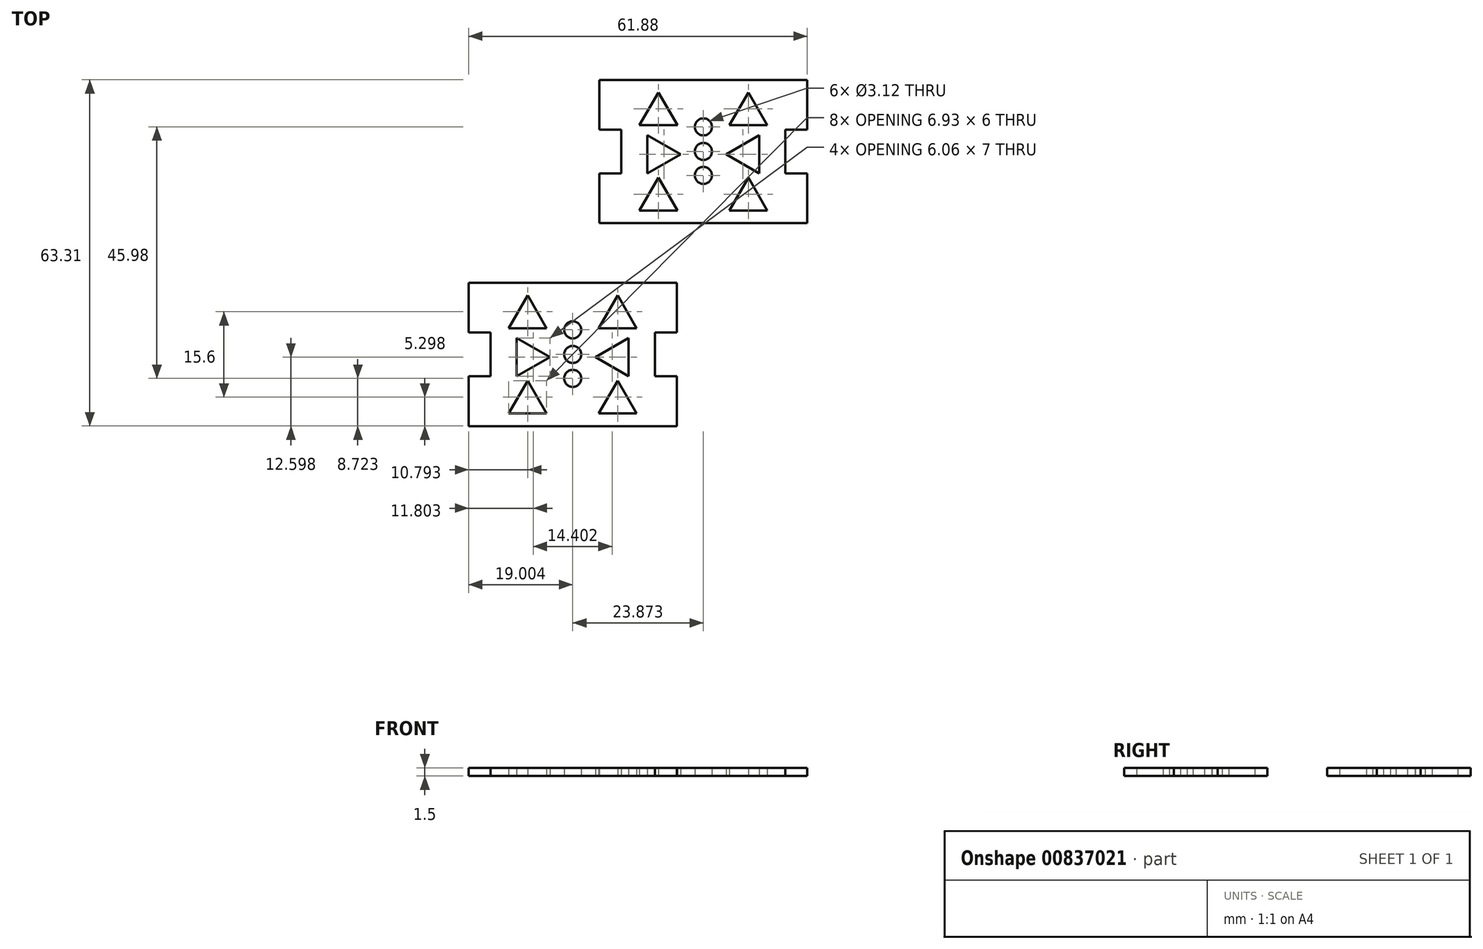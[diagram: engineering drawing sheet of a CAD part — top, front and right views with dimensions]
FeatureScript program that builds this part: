
annotation { "Feature Type Name" : "Feature", "Feature Type Description" : "" }
export const myFeature = defineFeature(function(context is Context, id is Id, definition is map)
    precondition{}
    {
        {
            var Q0;
            Q0=qCreatedBy(makeId("Top.planeOp"),FACE);
            var sketch = newSketch(context, id + "F0", { "sketchPlane" : qUnion([Q0])});
            skLineSegment(sketch, "E0.bottom", {"start": v(-70.41, 59.77) * mm, "end": v(-66.41, 59.77) * mm});
            skLineSegment(sketch, "E0.top", {"start": v(-70.41, 50.67) * mm, "end": v(-66.41, 50.67) * mm});
            skLineSegment(sketch, "E0.left", {"start": v(-70.41, 59.77) * mm, "end": v(-70.41, 50.67) * mm});
            skLineSegment(sketch, "E0.right", {"start": v(-66.41, 59.77) * mm, "end": v(-66.41, 50.67) * mm});
            skLineSegment(sketch, "E1", {"start": v(-66.41, 50.67) * mm, "end": v(-66.41, 42.67) * mm});
            skLineSegment(sketch, "E2.bottom", {"start": v(-70.41, 42.67) * mm, "end": v(-66.41, 42.67) * mm});
            skLineSegment(sketch, "E2.top", {"start": v(-70.41, 33.57) * mm, "end": v(-66.41, 33.57) * mm});
            skLineSegment(sketch, "E2.left", {"start": v(-70.41, 42.67) * mm, "end": v(-70.41, 33.57) * mm});
            skLineSegment(sketch, "E2.right", {"start": v(-66.41, 42.67) * mm, "end": v(-66.41, 33.57) * mm});
            skLineSegment(sketch, "E3.bottom", {"start": v(-66.41, 59.77) * mm, "end": v(-51.41, 59.77) * mm});
            skLineSegment(sketch, "E3.top", {"start": v(-66.41, 33.57) * mm, "end": v(-51.41, 33.57) * mm});
            skLineSegment(sketch, "E3.left", {"start": v(-66.41, 59.77) * mm, "end": v(-66.41, 33.57) * mm});
            skArc(sketch, "E4", {"start": v(-51.41, 52.73) * mm, "mid": v(-52.98, 51.16) * mm, "end": v(-51.41, 49.6) * mm});
            skArc(sketch, "E5", {"start": v(-51.41, 43.85) * mm, "mid": v(-52.98, 42.3) * mm, "end": v(-51.41, 40.73) * mm});
            skArc(sketch, "E6", {"start": v(-51.41, 48.23) * mm, "mid": v(-52.98, 46.67) * mm, "end": v(-51.41, 45.1) * mm});
            skLineSegment(sketch, "E7", {"start": v(-51.41, 59.77) * mm, "end": v(-51.41, 33.57) * mm});
            skPoint(sketch, "E3.right.end.orphan", {"position": v(-36.41, 33.57) * mm});
            skPoint(sketch, "E8.orphan", {"position": v(-36.41, 59.77) * mm});
            skCircle(sketch, "E9.cCircle", {"center": v(-59.62, 53.47) * mm, "radius": 2 * mm, "construction": true});
            skLineSegment(sketch, "E9.0", {"start": v(-56.16, 51.47) * mm, "end": v(-63.09, 51.47) * mm});
            skLineSegment(sketch, "E9.1", {"start": v(-63.09, 51.47) * mm, "end": v(-59.62, 57.47) * mm});
            skLineSegment(sketch, "E9.2", {"start": v(-59.62, 57.47) * mm, "end": v(-56.16, 51.47) * mm});
            skPoint(sketch, "E9.0.midPoint", {"position": v(-59.62, 51.47) * mm});
            skCircle(sketch, "E10.cCircle", {"center": v(-59.62, 37.87) * mm, "radius": 2 * mm, "construction": true});
            skLineSegment(sketch, "E10.0", {"start": v(-56.16, 35.87) * mm, "end": v(-63.09, 35.87) * mm});
            skLineSegment(sketch, "E10.1", {"start": v(-63.09, 35.87) * mm, "end": v(-59.62, 41.87) * mm});
            skLineSegment(sketch, "E10.2", {"start": v(-59.62, 41.87) * mm, "end": v(-56.16, 35.87) * mm});
            skPoint(sketch, "E10.0.midPoint", {"position": v(-59.62, 35.87) * mm});
            skCircle(sketch, "E11.cCircle", {"center": v(-59.62, 46.17) * mm, "radius": 2.02 * mm, "construction": true});
            skLineSegment(sketch, "E11.0", {"start": v(-55.58, 46.17) * mm, "end": v(-61.65, 42.67) * mm});
            skLineSegment(sketch, "E11.1", {"start": v(-61.65, 42.67) * mm, "end": v(-61.65, 49.67) * mm});
            skLineSegment(sketch, "E11.2", {"start": v(-61.65, 49.67) * mm, "end": v(-55.58, 46.17) * mm});
            skPoint(sketch, "E11.0.midPoint", {"position": v(-58.61, 44.42) * mm});
            skLineSegment(sketch, "E12.MirrorCS", {"start": v(-36.41, 59.77) * mm, "end": v(-36.41, 50.67) * mm});
            skLineSegment(sketch, "E13.MirrorCS", {"start": v(-36.41, 42.67) * mm, "end": v(-36.41, 33.57) * mm});
            skLineSegment(sketch, "E14.MirrorCS", {"start": v(-36.41, 50.67) * mm, "end": v(-36.41, 42.67) * mm});
            skLineSegment(sketch, "E15.MirrorCS", {"start": v(-32.41, 42.67) * mm, "end": v(-32.41, 33.57) * mm});
            skLineSegment(sketch, "E16.MirrorCS", {"start": v(-39.74, 51.47) * mm, "end": v(-43.2, 57.47) * mm});
            skLineSegment(sketch, "E17.MirrorCS", {"start": v(-32.41, 50.67) * mm, "end": v(-36.41, 50.67) * mm});
            skLineSegment(sketch, "E18.MirrorCS", {"start": v(-39.74, 35.87) * mm, "end": v(-43.2, 41.87) * mm});
            skLineSegment(sketch, "E19.MirrorCS", {"start": v(-32.41, 59.77) * mm, "end": v(-32.41, 50.67) * mm});
            skLineSegment(sketch, "E20.MirrorCS", {"start": v(-41.18, 42.67) * mm, "end": v(-41.18, 49.67) * mm});
            skCircle(sketch, "E21.MirrorC", {"center": v(-43.2, 46.17) * mm, "radius": 2.02 * mm, "construction": true});
            skLineSegment(sketch, "E22.MirrorCS", {"start": v(-36.41, 59.77) * mm, "end": v(-36.41, 33.57) * mm});
            skArc(sketch, "E23.MirrorCS", {"start": v(-51.41, 52.73) * mm, "mid": v(-49.85, 51.16) * mm, "end": v(-51.41, 49.6) * mm});
            skCircle(sketch, "E24.MirrorC", {"center": v(-43.2, 53.47) * mm, "radius": 2 * mm, "construction": true});
            skLineSegment(sketch, "E25.MirrorCS", {"start": v(-32.41, 33.57) * mm, "end": v(-36.41, 33.57) * mm});
            skLineSegment(sketch, "E26.MirrorCS", {"start": v(-43.2, 57.47) * mm, "end": v(-46.67, 51.47) * mm});
            skLineSegment(sketch, "E27.MirrorCS", {"start": v(-32.41, 59.77) * mm, "end": v(-36.41, 59.77) * mm});
            skLineSegment(sketch, "E28.MirrorCS", {"start": v(-43.2, 41.87) * mm, "end": v(-46.67, 35.87) * mm});
            skCircle(sketch, "E29.MirrorC", {"center": v(-43.2, 37.87) * mm, "radius": 2 * mm, "construction": true});
            skLineSegment(sketch, "E30.MirrorCS", {"start": v(-41.18, 49.67) * mm, "end": v(-47.24, 46.17) * mm});
            skLineSegment(sketch, "E31.MirrorCS", {"start": v(-36.41, 59.77) * mm, "end": v(-51.41, 59.77) * mm});
            skPoint(sketch, "E32.MirrorP", {"position": v(-44.21, 44.42) * mm});
            skPoint(sketch, "E33.MirrorP", {"position": v(-43.2, 51.47) * mm});
            skLineSegment(sketch, "E34.MirrorCS", {"start": v(-32.41, 42.67) * mm, "end": v(-36.41, 42.67) * mm});
            skLineSegment(sketch, "E35.MirrorCS", {"start": v(-47.24, 46.17) * mm, "end": v(-41.18, 42.67) * mm});
            skLineSegment(sketch, "E36.MirrorCS", {"start": v(-36.41, 33.57) * mm, "end": v(-51.41, 33.57) * mm});
            skPoint(sketch, "E37.MirrorP", {"position": v(-43.2, 35.87) * mm});
            skLineSegment(sketch, "E38.MirrorCS", {"start": v(-46.67, 35.87) * mm, "end": v(-39.74, 35.87) * mm});
            skArc(sketch, "E39.MirrorCS", {"start": v(-51.41, 48.23) * mm, "mid": v(-49.85, 46.67) * mm, "end": v(-51.41, 45.1) * mm});
            skLineSegment(sketch, "E40.MirrorCS", {"start": v(-46.67, 51.47) * mm, "end": v(-39.74, 51.47) * mm});
            skArc(sketch, "E41.MirrorCS", {"start": v(-51.41, 43.85) * mm, "mid": v(-49.85, 42.3) * mm, "end": v(-51.41, 40.73) * mm});
            skLineSegment(sketch, "E42.bottom", {"start": v(-94.29, 22.66) * mm, "end": v(-90.29, 22.66) * mm});
            skLineSegment(sketch, "E42.top", {"start": v(-94.29, 13.56) * mm, "end": v(-90.29, 13.56) * mm});
            skLineSegment(sketch, "E42.left", {"start": v(-94.29, 22.66) * mm, "end": v(-94.29, 13.56) * mm});
            skLineSegment(sketch, "E42.right", {"start": v(-90.29, 22.66) * mm, "end": v(-90.29, 13.56) * mm});
            skLineSegment(sketch, "E43", {"start": v(-90.29, 13.56) * mm, "end": v(-90.29, 5.56) * mm});
            skLineSegment(sketch, "E44.bottom", {"start": v(-94.29, 5.56) * mm, "end": v(-90.29, 5.56) * mm});
            skLineSegment(sketch, "E44.top", {"start": v(-94.29, -3.54) * mm, "end": v(-90.29, -3.54) * mm});
            skLineSegment(sketch, "E44.left", {"start": v(-94.29, 5.56) * mm, "end": v(-94.29, -3.54) * mm});
            skLineSegment(sketch, "E44.right", {"start": v(-90.29, 5.56) * mm, "end": v(-90.29, -3.54) * mm});
            skLineSegment(sketch, "E45.bottom", {"start": v(-90.29, 22.66) * mm, "end": v(-75.29, 22.66) * mm});
            skLineSegment(sketch, "E45.top", {"start": v(-90.29, -3.54) * mm, "end": v(-75.29, -3.54) * mm});
            skLineSegment(sketch, "E45.left", {"start": v(-90.29, 22.66) * mm, "end": v(-90.29, -3.54) * mm});
            skArc(sketch, "E46", {"start": v(-75.29, 15.62) * mm, "mid": v(-76.85, 14.05) * mm, "end": v(-75.29, 12.5) * mm});
            skArc(sketch, "E47", {"start": v(-75.29, 6.75) * mm, "mid": v(-76.85, 5.18) * mm, "end": v(-75.29, 3.62) * mm});
            skArc(sketch, "E48", {"start": v(-75.29, 11.12) * mm, "mid": v(-76.85, 9.56) * mm, "end": v(-75.29, 8) * mm});
            skLineSegment(sketch, "E49", {"start": v(-75.29, 22.66) * mm, "end": v(-75.29, -3.54) * mm});
            skPoint(sketch, "E45.right.end.orphan", {"position": v(-60.29, -3.54) * mm});
            skPoint(sketch, "E50.orphan", {"position": v(-60.29, 22.66) * mm});
            skCircle(sketch, "E51.cCircle", {"center": v(-83.5, 16.36) * mm, "radius": 2 * mm, "construction": true});
            skLineSegment(sketch, "E51.0", {"start": v(-80.03, 14.36) * mm, "end": v(-86.96, 14.36) * mm});
            skLineSegment(sketch, "E51.1", {"start": v(-86.96, 14.36) * mm, "end": v(-83.5, 20.36) * mm});
            skLineSegment(sketch, "E51.2", {"start": v(-83.5, 20.36) * mm, "end": v(-80.03, 14.36) * mm});
            skPoint(sketch, "E51.0.midPoint", {"position": v(-83.5, 14.36) * mm});
            skCircle(sketch, "E52.cCircle", {"center": v(-83.5, 0.76) * mm, "radius": 2 * mm, "construction": true});
            skLineSegment(sketch, "E52.0", {"start": v(-80.03, -1.24) * mm, "end": v(-86.96, -1.24) * mm});
            skLineSegment(sketch, "E52.1", {"start": v(-86.96, -1.24) * mm, "end": v(-83.5, 4.76) * mm});
            skLineSegment(sketch, "E52.2", {"start": v(-83.5, 4.76) * mm, "end": v(-80.03, -1.24) * mm});
            skPoint(sketch, "E52.0.midPoint", {"position": v(-83.5, -1.24) * mm});
            skCircle(sketch, "E53.cCircle", {"center": v(-83.5, 9.06) * mm, "radius": 2.02 * mm, "construction": true});
            skLineSegment(sketch, "E53.0", {"start": v(-79.46, 9.06) * mm, "end": v(-85.52, 5.56) * mm});
            skLineSegment(sketch, "E53.1", {"start": v(-85.52, 5.56) * mm, "end": v(-85.52, 12.56) * mm});
            skLineSegment(sketch, "E53.2", {"start": v(-85.52, 12.56) * mm, "end": v(-79.46, 9.06) * mm});
            skPoint(sketch, "E53.0.midPoint", {"position": v(-82.49, 7.3) * mm});
            skLineSegment(sketch, "E54.MirrorCS", {"start": v(-60.29, 22.66) * mm, "end": v(-60.29, 13.56) * mm});
            skLineSegment(sketch, "E55.MirrorCS", {"start": v(-60.29, 5.56) * mm, "end": v(-60.29, -3.54) * mm});
            skLineSegment(sketch, "E56.MirrorCS", {"start": v(-60.29, 13.56) * mm, "end": v(-60.29, 5.56) * mm});
            skLineSegment(sketch, "E57.MirrorCS", {"start": v(-56.29, 5.56) * mm, "end": v(-56.29, -3.54) * mm});
            skLineSegment(sketch, "E58.MirrorCS", {"start": v(-63.61, 14.36) * mm, "end": v(-67.07, 20.36) * mm});
            skLineSegment(sketch, "E59.MirrorCS", {"start": v(-56.29, 13.56) * mm, "end": v(-60.29, 13.56) * mm});
            skLineSegment(sketch, "E60.MirrorCS", {"start": v(-63.61, -1.24) * mm, "end": v(-67.07, 4.76) * mm});
            skLineSegment(sketch, "E61.MirrorCS", {"start": v(-56.29, 22.66) * mm, "end": v(-56.29, 13.56) * mm});
            skLineSegment(sketch, "E62.MirrorCS", {"start": v(-65.05, 5.56) * mm, "end": v(-65.05, 12.56) * mm});
            skCircle(sketch, "E63.MirrorC", {"center": v(-67.07, 9.06) * mm, "radius": 2.02 * mm, "construction": true});
            skLineSegment(sketch, "E64.MirrorCS", {"start": v(-60.29, 22.66) * mm, "end": v(-60.29, -3.54) * mm});
            skArc(sketch, "E65.MirrorCS", {"start": v(-75.29, 15.62) * mm, "mid": v(-73.72, 14.05) * mm, "end": v(-75.29, 12.5) * mm});
            skCircle(sketch, "E66.MirrorC", {"center": v(-67.07, 16.36) * mm, "radius": 2 * mm, "construction": true});
            skLineSegment(sketch, "E67.MirrorCS", {"start": v(-56.29, -3.54) * mm, "end": v(-60.29, -3.54) * mm});
            skLineSegment(sketch, "E68.MirrorCS", {"start": v(-67.07, 20.36) * mm, "end": v(-70.54, 14.36) * mm});
            skLineSegment(sketch, "E69.MirrorCS", {"start": v(-56.29, 22.66) * mm, "end": v(-60.29, 22.66) * mm});
            skLineSegment(sketch, "E70.MirrorCS", {"start": v(-67.07, 4.76) * mm, "end": v(-70.54, -1.24) * mm});
            skCircle(sketch, "E71.MirrorC", {"center": v(-67.07, 0.76) * mm, "radius": 2 * mm, "construction": true});
            skLineSegment(sketch, "E72.MirrorCS", {"start": v(-65.05, 12.56) * mm, "end": v(-71.12, 9.06) * mm});
            skLineSegment(sketch, "E73.MirrorCS", {"start": v(-60.29, 22.66) * mm, "end": v(-75.29, 22.66) * mm});
            skPoint(sketch, "E74.MirrorP", {"position": v(-68.09, 7.3) * mm});
            skPoint(sketch, "E75.MirrorP", {"position": v(-67.07, 14.36) * mm});
            skLineSegment(sketch, "E76.MirrorCS", {"start": v(-56.29, 5.56) * mm, "end": v(-60.29, 5.56) * mm});
            skLineSegment(sketch, "E77.MirrorCS", {"start": v(-71.12, 9.06) * mm, "end": v(-65.05, 5.56) * mm});
            skLineSegment(sketch, "E78.MirrorCS", {"start": v(-60.29, -3.54) * mm, "end": v(-75.29, -3.54) * mm});
            skPoint(sketch, "E79.MirrorP", {"position": v(-67.07, -1.24) * mm});
            skLineSegment(sketch, "E80.MirrorCS", {"start": v(-70.54, -1.24) * mm, "end": v(-63.61, -1.24) * mm});
            skArc(sketch, "E81.MirrorCS", {"start": v(-75.29, 11.12) * mm, "mid": v(-73.72, 9.56) * mm, "end": v(-75.29, 8) * mm});
            skLineSegment(sketch, "E82.MirrorCS", {"start": v(-70.54, 14.36) * mm, "end": v(-63.61, 14.36) * mm});
            skArc(sketch, "E83.MirrorCS", {"start": v(-75.29, 6.75) * mm, "mid": v(-73.72, 5.18) * mm, "end": v(-75.29, 3.62) * mm});
            skSolve(sketch);
        }
        {
            var Q0;
            {var subQ0=sQuery(id+"F0.wireOp",EDGE,"E0.bottom");Q0=makeQuery(id+"F0.imprint","IMPRINT",FACE,{"disambiguationData":[TD([[makeQuery(id+"F0.imprint","IMPRINT",EDGE,{"derivedFrom":subQ0}),-1.0]])]});}
            var Q1;
            {var subQ1=sQuery(id+"F0.wireOp",EDGE,"E2.bottom");Q1=makeQuery(id+"F0.imprint","IMPRINT",FACE,{"disambiguationData":[TD([[makeQuery(id+"F0.imprint","IMPRINT",EDGE,{"derivedFrom":subQ1}),-1.0]])]});}
            var Q2;
            {var subQ5=sQuery(id+"F0.wireOp",EDGE,"E3.bottom");Q2=makeQuery(id+"F0.imprint","IMPRINT",FACE,{"disambiguationData":[TD([[makeQuery(id+"F0.imprint","IMPRINT",EDGE,{"derivedFrom":subQ5}),-1.0]])]});}
            var Q3;
            Q3=makeQuery(id+"F0.imprint","IMPRINT",FACE,{"disambiguationData":[TD([[makeQuery(id+"F0.imprint","IMPRINT",EDGE,{"derivedFrom":sQuery(id+"F0.wireOp",EDGE,"E16.MirrorCS")}),-1.0]])]});
            var Q4;
            {var subQ1=sQuery(id+"F0.wireOp",EDGE,"E13.MirrorCS");Q4=makeQuery(id+"F0.imprint","IMPRINT",FACE,{"disambiguationData":[TD([[makeQuery(id+"F0.imprint","IMPRINT",EDGE,{"derivedFrom":subQ1}),1.0]])]});}
            var Q5;
            {var subQ0=sQuery(id+"F0.wireOp",EDGE,"E17.MirrorCS");Q5=makeQuery(id+"F0.imprint","IMPRINT",FACE,{"disambiguationData":[TD([[makeQuery(id+"F0.imprint","IMPRINT",EDGE,{"derivedFrom":subQ0}),-1.0]])]});}
            extrude(context, id + "F1", {"entities" : qUnion([Q0, Q1, Q2, Q3, Q4, Q5]), "depth" : 1.5 * mm, "offsetDistance" : 25.4 * mm});
        }
        {
            var Q0;
            {var subQ0=sQuery(id+"F0.wireOp",EDGE,"E42.bottom");Q0=makeQuery(id+"F0.imprint","IMPRINT",FACE,{"disambiguationData":[TD([[makeQuery(id+"F0.imprint","IMPRINT",EDGE,{"derivedFrom":subQ0}),-1.0]])]});}
            var Q1;
            {var subQ5=sQuery(id+"F0.wireOp",EDGE,"E45.bottom");Q1=makeQuery(id+"F0.imprint","IMPRINT",FACE,{"disambiguationData":[TD([[makeQuery(id+"F0.imprint","IMPRINT",EDGE,{"derivedFrom":subQ5}),-1.0]])]});}
            var Q2;
            {var subQ1=sQuery(id+"F0.wireOp",EDGE,"E44.bottom");Q2=makeQuery(id+"F0.imprint","IMPRINT",FACE,{"disambiguationData":[TD([[makeQuery(id+"F0.imprint","IMPRINT",EDGE,{"derivedFrom":subQ1}),-1.0]])]});}
            var Q3;
            Q3=makeQuery(id+"F0.imprint","IMPRINT",FACE,{"disambiguationData":[TD([[makeQuery(id+"F0.imprint","IMPRINT",EDGE,{"derivedFrom":sQuery(id+"F0.wireOp",EDGE,"E58.MirrorCS")}),-1.0]])]});
            var Q4;
            {var subQ1=sQuery(id+"F0.wireOp",EDGE,"E55.MirrorCS");Q4=makeQuery(id+"F0.imprint","IMPRINT",FACE,{"disambiguationData":[TD([[makeQuery(id+"F0.imprint","IMPRINT",EDGE,{"derivedFrom":subQ1}),1.0]])]});}
            var Q5;
            {var subQ0=sQuery(id+"F0.wireOp",EDGE,"E59.MirrorCS");Q5=makeQuery(id+"F0.imprint","IMPRINT",FACE,{"disambiguationData":[TD([[makeQuery(id+"F0.imprint","IMPRINT",EDGE,{"derivedFrom":subQ0}),-1.0]])]});}
            extrude(context, id + "F2", {"entities" : qUnion([Q0, Q1, Q2, Q3, Q4, Q5]), "depth" : 1.5 * mm, "offsetDistance" : 25.4 * mm});
        }
    });
